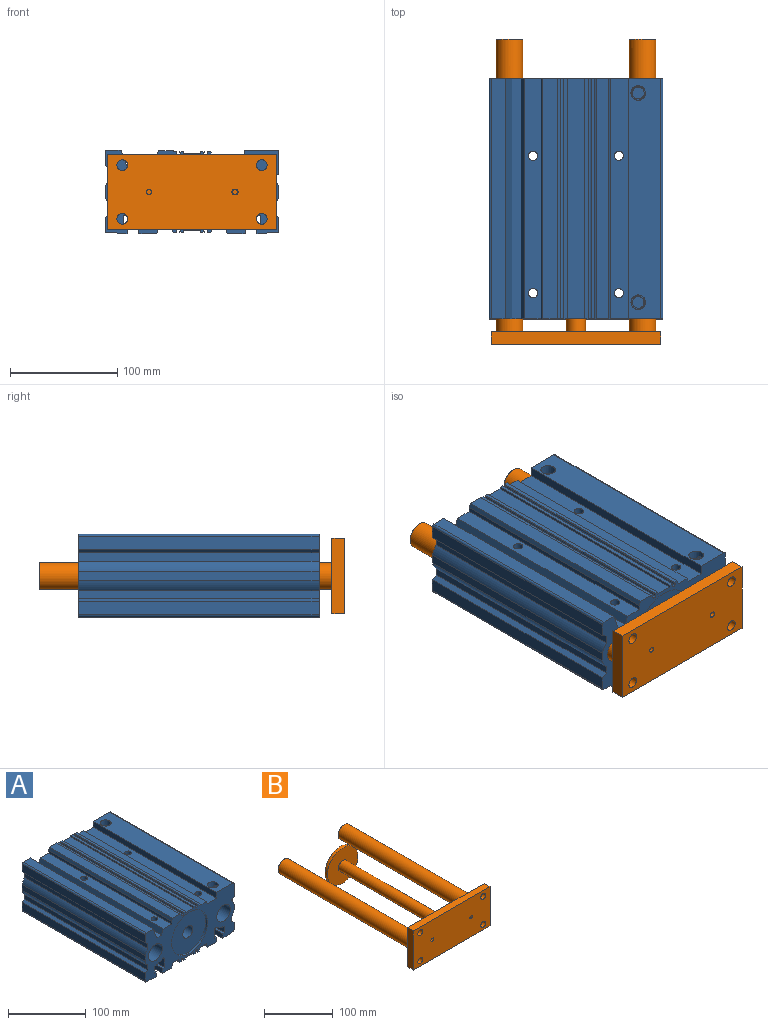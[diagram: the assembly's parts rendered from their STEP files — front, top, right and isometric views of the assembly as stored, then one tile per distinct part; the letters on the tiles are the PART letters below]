
ASSEMBLY  parts=2 mates=1
PART A: 165 faces, bbox 162.1x224.1x78.1 mm
  f0: cylinder r=4.3mm len=49mm, axis (0,0,1), area 1323.9mm2, adj f103,f137
  f1: cylinder r=4.3mm len=49mm, axis (0,0,1), area 1323.9mm2, adj f109,f135
  f2: cylinder r=4.3mm len=49mm, axis (0,0,1), area 1323.9mm2, adj f103,f133
  f3: cylinder r=4.3mm len=49mm, axis (0,0,1), area 1323.9mm2, adj f109,f131
  f4: plane 162x78mm, normal (0,-1,0), area 6470mm2, adj f6,f7,f8,f9,f10,f11,f12,f13
  f5: plane 162x78mm, normal (0,1,0), area 6312.6mm2, adj f6,f7,f8,f9,f10,f11,f12,f13
  f6: plane 224x12.5mm, normal (1,0,0), area 2800mm2, adj f4,f5,f69,f128
  f7: plane 224x9mm, normal (0,0,-1), area 2016mm2, adj f4,f5,f25,f125
  f8: plane 224x16.5mm, normal (0,0,-1), area 3519.3mm2, adj f4,f5,f34,f122,f134,f138,f139
  f9: plane 224x0.74mm, normal (-1,0,0), area 165.7mm2, adj f4,f5,f51,f119
  f10: plane 224x0.74mm, normal (1,0,0), area 165.7mm2, adj f4,f5,f51,f118
  f11: plane 224x2.2mm, normal (-1,0,0), area 492.8mm2, adj f4,f5,f59,f118
  f12: plane 224x8.78mm, normal (1,0,0), area 1965.6mm2, adj f4,f5,f67,f68
  f13: plane 224x8.78mm, normal (-1,0,0), area 1965.6mm2, adj f4,f5,f60,f63
  f14: plane 224x12.5mm, normal (-1,0,0), area 2800mm2, adj f4,f5,f65,f127
  f15: plane 224x16.5mm, normal (0,0,-1), area 3514.3mm2, adj f4,f5,f35,f114,f132,f136,f141,f142
  f16: plane 224x30mm, normal (0,0,1), area 6428.4mm2, adj f4,f5,f102,f129,f152,f156
  f17: plane 224x13mm, normal (0,0,1), area 2912mm2, adj f4,f5,f112,f130
  f18: plane 224x9mm, normal (0,0,-1), area 2016mm2, adj f4,f5,f44,f124
  f19: plane 224x20.5mm, normal (1,0,0), area 4296.5mm2, adj f4,f5,f66,f129,f160,f164
  f20: plane 224x12.5mm, normal (-1,0,0), area 2800mm2, adj f4,f5,f61,f130
  f21: cylinder r=12.53mm len=224mm, axis (0,-1,0), area 17628.1mm2, adj f4,f5
  f22: cylinder r=12.53mm len=224mm, axis (0,-1,0), area 17628.1mm2, adj f4,f5
  f23: cylinder r=2.5mm len=8mm, axis (0,1,0), area 125.7mm2, adj f5,f24
  f24: plane 5x5mm, normal (0,1,0), area 19.6mm2, adj f23
  f25: plane 224x7.5mm, normal (-1,0,0), area 1680mm2, adj f4,f5,f7,f26
  f26: plane 224x3.4mm, normal (0,0,1), area 761.6mm2, adj f4,f5,f25,f27
  f27: plane 224x10mm, normal (-1,0,0), area 2240mm2, adj f4,f5,f26,f28
  f28: plane 224x3.4mm, normal (0,0,-1), area 761.6mm2, adj f4,f5,f27,f29
  f29: plane 224x1.06mm, normal (-1,0,0), area 236.3mm2, adj f4,f5,f28,f30
  f30: cylinder r=20.5mm len=224mm, axis (0,1,0), area 2721.6mm2, adj f4,f5,f29,f31
  f31: cylinder r=2mm len=224mm, axis (0,1,0), area 1002mm2, adj f4,f5,f30,f32
  f32: plane 224x13.81mm, normal (1,0,0), area 3092.8mm2, adj f4,f5,f31,f33
  f33: plane 224x3.4mm, normal (0,0,1), area 761.6mm2, adj f4,f5,f32,f34
  f34: plane 224x7.5mm, normal (1,0,0), area 1680mm2, adj f4,f5,f8,f33
  f35: plane 224x7.5mm, normal (-1,0,0), area 1680mm2, adj f4,f5,f15,f36
  f36: plane 224x3.4mm, normal (0,0,1), area 761.6mm2, adj f4,f5,f35,f37
  f37: plane 224x13.81mm, normal (-1,0,0), area 3092.8mm2, adj f4,f5,f36,f38
  f38: cylinder r=2mm len=224mm, axis (0,1,0), area 1002mm2, adj f4,f5,f37,f39
  f39: cylinder r=20.5mm len=224mm, axis (0,1,0), area 2721.6mm2, adj f4,f5,f38,f40
  f40: plane 224x1.06mm, normal (1,0,0), area 236.3mm2, adj f4,f5,f39,f41
  f41: plane 224x3.4mm, normal (0,0,-1), area 761.6mm2, adj f4,f5,f40,f42
  f42: plane 224x10mm, normal (1,0,0), area 2240mm2, adj f4,f5,f41,f43
  f43: plane 224x3.4mm, normal (0,0,1), area 761.6mm2, adj f4,f5,f42,f44
  f44: plane 224x7.5mm, normal (1,0,0), area 1680mm2, adj f4,f5,f18,f43
  f45: cylinder r=2.02mm len=224mm, axis (0,-1,0), area 2093.3mm2, adj f4,f5,f46,f47
  f46: plane 224x0.74mm, normal (1,0,0), area 165.7mm2, adj f4,f5,f45,f104
  f47: plane 224x0.74mm, normal (-1,0,0), area 165.7mm2, adj f4,f5,f45,f97
  f48: cylinder r=2.02mm len=224mm, axis (0,-1,0), area 2093.3mm2, adj f4,f5,f49,f50
  f49: plane 224x0.74mm, normal (1,0,0), area 165.7mm2, adj f4,f5,f48,f96
  f50: plane 224x0.74mm, normal (-1,0,0), area 165.7mm2, adj f4,f5,f48,f98
  f51: cylinder r=2.02mm len=224mm, axis (0,-1,0), area 2093.3mm2, adj f4,f5,f9,f10
  f52: cylinder r=2.02mm len=224mm, axis (0,-1,0), area 2093.3mm2, adj f4,f5,f53,f54
  f53: plane 224x0.74mm, normal (-1,0,0), area 165.7mm2, adj f4,f5,f52,f113
  f54: plane 224x0.74mm, normal (1,0,0), area 165.7mm2, adj f4,f5,f52,f117
  f55: plane 224x2.2mm, normal (1,0,0), area 492.8mm2, adj f4,f5,f57,f97
  f56: plane 224x2.2mm, normal (-1,0,0), area 492.8mm2, adj f4,f5,f57,f96
  f57: plane 224x16mm, normal (0,0,1), area 3584mm2, adj f4,f5,f55,f56
  f58: plane 224x2.2mm, normal (1,0,0), area 492.8mm2, adj f4,f5,f59,f113
  f59: plane 224x16mm, normal (0,0,-1), area 3584mm2, adj f4,f5,f11,f58
  f60: cylinder r=19.5mm len=224mm, axis (0,-1,0), area 2371.8mm2, adj f4,f5,f13,f62
  f61: plane 224x5mm, normal (-0.5,0,-0.87), area 1293.3mm2, adj f4,f5,f20,f62
  f62: plane 224x8.04mm, normal (-1,0,0), area 1800.8mm2, adj f4,f5,f60,f61
  f63: cylinder r=19.5mm len=224mm, axis (0,-1,0), area 2371.8mm2, adj f4,f5,f13,f64
  f64: plane 224x7.04mm, normal (-1,0,0), area 1576.8mm2, adj f4,f5,f63,f65
  f65: plane 224x5mm, normal (-0.5,0,0.87), area 1293.3mm2, adj f4,f5,f14,f64
  f66: plane 224x2.93mm, normal (0.5,0,-0.87), area 758.5mm2, adj f4,f5,f19,f71
  f67: cylinder r=19.5mm len=224mm, axis (0,-1,0), area 1864.1mm2, adj f4,f5,f12,f71
  f68: cylinder r=19.5mm len=224mm, axis (0,-1,0), area 2371.8mm2, adj f4,f5,f12,f70
  f69: plane 224x5mm, normal (0.5,0,0.87), area 1293.3mm2, adj f4,f5,f6,f70
  f70: plane 224x7.04mm, normal (1,0,0), area 1576.8mm2, adj f4,f5,f68,f69
  f71: cylinder r=2mm len=224mm, axis (0,-1,0), area 762mm2, adj f4,f5,f66,f67
  f72: cylinder r=31.5mm len=63mm, axis (0,1,0), area 613.6mm2, adj f5,f73
  f73: plane 63x63mm, normal (0,1,0), area 3117.2mm2, adj f72
  f74: cylinder r=32.5mm len=65mm, axis (0,-1,0), area 633mm2, adj f4,f75
  f75: plane 65x65mm, normal (0,-1,0), area 3062.4mm2, adj f74,f79
  f76: plane 63x63mm, normal (0,-1,0), area 3117.2mm2, adj f77
  f77: cylinder r=31.5mm len=180mm, axis (0,-1,0), area 35625.7mm2, adj f76,f78
  f78: plane 63x63mm, normal (0,1,0), area 2861.4mm2, adj f77,f79
  f79: cylinder r=9.03mm len=18.9mm, axis (0,1,0), area 1071.7mm2, adj f75,f78
  f80: cylinder r=5mm len=22mm, axis (0,1,0), area 691.2mm2, adj f5,f81
  f81: plane 10x10mm, normal (0,1,0), area 78.5mm2, adj f80
  f82: cylinder r=5mm len=22mm, axis (0,1,0), area 691.2mm2, adj f5,f83
  f83: plane 10x10mm, normal (0,1,0), area 78.5mm2, adj f82
  f84: cylinder r=5mm len=22mm, axis (0,1,0), area 691.2mm2, adj f5,f85
  f85: plane 10x10mm, normal (0,1,0), area 78.5mm2, adj f84
  f86: cylinder r=5mm len=22mm, axis (0,1,0), area 691.2mm2, adj f5,f87
  f87: plane 10x10mm, normal (0,1,0), area 78.5mm2, adj f86
  f88: plane 4x1mm, normal (0,0,-1), area 4mm2, adj f5,f90,f91,f92,f93
  f89: plane 4x1mm, normal (0,0,1), area 4mm2, adj f5,f90,f91,f92,f93
  f90: plane 5x3mm, normal (0,1,0), area 2.5mm2, adj f88,f89,f92,f95
  f91: plane 5x3mm, normal (0,1,0), area 2.5mm2, adj f88,f89,f93,f95
  f92: cylinder r=2.5mm len=5mm, axis (0,1,0), area 31.4mm2, adj f5,f88,f89,f90
  f93: cylinder r=2.5mm len=5mm, axis (0,1,0), area 31.4mm2, adj f5,f88,f89,f91
  f94: plane 5x5mm, normal (0,1,0), area 19.6mm2, adj f95
  f95: cylinder r=2.5mm len=5mm, axis (0,1,0), area 62.8mm2, adj f90,f91,f94
  f96: plane 224x3.2mm, normal (0,0,1), area 716.8mm2, adj f4,f5,f49,f56
  f97: plane 224x3.2mm, normal (0,0,1), area 716.8mm2, adj f4,f5,f47,f55
  f98: plane 224x3.2mm, normal (0,0,1), area 716.8mm2, adj f4,f5,f50,f99
  f99: plane 224x3.7mm, normal (0.94,0,0.34), area 882mm2, adj f4,f5,f98,f100
  f100: plane 224x11.75mm, normal (0,0,1), area 2632.7mm2, adj f4,f5,f99,f101
  f101: plane 224x4mm, normal (0.94,0,0.34), area 953.5mm2, adj f4,f5,f100,f103
  f102: plane 224x9mm, normal (-1,0,0), area 2016mm2, adj f4,f5,f16,f103
  f103: plane 224x17.04mm, normal (0,0,1), area 3701.7mm2, adj f0,f2,f4,f5,f101,f102
  f104: plane 224x3.2mm, normal (0,0,1), area 716.8mm2, adj f4,f5,f46,f105
  f105: plane 224x0.8mm, normal (1,0,0), area 179.2mm2, adj f4,f5,f104,f106
  f106: plane 224x13.6mm, normal (0,0,1), area 3046.4mm2, adj f4,f5,f105,f107
  f107: plane 224x4.12mm, normal (-0.94,0,0.34), area 982.4mm2, adj f4,f5,f106,f108
  f108: plane 224x4.38mm, normal (-1,0,0), area 980.8mm2, adj f4,f5,f107,f109
  f109: plane 224x15.5mm, normal (0,0,1), area 3355.8mm2, adj f1,f3,f4,f5,f108,f110
  f110: plane 224x8mm, normal (-0.94,0,0.34), area 1907mm2, adj f4,f5,f109,f111
  f111: plane 224x8.9mm, normal (0,0,1), area 1993.8mm2, adj f4,f5,f110,f112
  f112: plane 224x17mm, normal (0.94,0,0.34), area 4052.4mm2, adj f4,f5,f17,f111
  f113: plane 224x3.2mm, normal (0,0,-1), area 716.8mm2, adj f4,f5,f53,f58
  f114: plane 224x6.5mm, normal (0.94,0,-0.34), area 1549.4mm2, adj f4,f5,f15,f115
  f115: plane 224x11.34mm, normal (0,0,-1), area 2540.5mm2, adj f4,f5,f114,f116
  f116: plane 224x5.2mm, normal (-0.94,0,-0.34), area 1239.6mm2, adj f4,f5,f115,f117
  f117: plane 224x3.2mm, normal (0,0,-1), area 716.8mm2, adj f4,f5,f54,f116
  f118: plane 224x3.2mm, normal (0,0,-1), area 716.8mm2, adj f4,f5,f10,f11
  f119: plane 224x3.2mm, normal (0,0,-1), area 716.8mm2, adj f4,f5,f9,f120
  f120: plane 224x5.2mm, normal (0.94,0,-0.34), area 1239.6mm2, adj f4,f5,f119,f121
  f121: plane 224x11.34mm, normal (0,0,-1), area 2540.5mm2, adj f4,f5,f120,f122
  f122: plane 224x6.5mm, normal (-0.94,0,-0.34), area 1549.4mm2, adj f4,f5,f8,f121
  f123: plane 224x8.92mm, normal (0,0,-1), area 1998.7mm2, adj f4,f5,f124,f127
  f124: plane 224x1mm, normal (-0.87,0,-0.5), area 258.7mm2, adj f4,f5,f18,f123
  f125: plane 224x1mm, normal (0.87,0,-0.5), area 258.7mm2, adj f4,f5,f7,f126
  f126: plane 224x8.92mm, normal (0,0,-1), area 1998.7mm2, adj f4,f5,f125,f128
  f127: cylinder r=2mm len=224mm, axis (0,-1,0), area 703.7mm2, adj f4,f5,f14,f123
  f128: cylinder r=2mm len=224mm, axis (0,1,0), area 703.7mm2, adj f4,f5,f6,f126
  f129: cylinder r=2mm len=224mm, axis (0,1,0), area 703.7mm2, adj f4,f5,f16,f19
  f130: cylinder r=2mm len=224mm, axis (0,1,0), area 703.7mm2, adj f4,f5,f17,f20
  f131: plane 10x10mm, normal (0,0,-1), area 20.5mm2, adj f3,f132
  f132: cylinder r=5mm len=20mm, axis (0,0,-1), area 628.3mm2, adj f15,f131
  f133: plane 10x10mm, normal (0,0,-1), area 20.5mm2, adj f2,f134
  f134: cylinder r=5mm len=20mm, axis (0,0,-1), area 628.3mm2, adj f8,f133
  f135: plane 10x10mm, normal (0,0,-1), area 20.5mm2, adj f1,f136
  f136: cylinder r=5mm len=20mm, axis (0,0,-1), area 628.3mm2, adj f15,f135
  f137: plane 10x10mm, normal (0,0,-1), area 20.5mm2, adj f0,f138
  f138: cylinder r=5mm len=20mm, axis (0,0,-1), area 628.3mm2, adj f8,f137
  f139: cylinder r=2.5mm len=8mm, axis (0,0,-1), area 125.7mm2, adj f8,f140
  f140: plane 5x5mm, normal (0,0,-1), area 19.6mm2, adj f139
  f141: plane 4x1mm, normal (0,1,0), area 4mm2, adj f15,f143,f144,f145,f146
  f142: plane 4x1mm, normal (0,-1,0), area 4mm2, adj f15,f143,f144,f145,f146
  f143: plane 5x3mm, normal (0,0,-1), area 2.5mm2, adj f141,f142,f145,f148
  f144: plane 5x3mm, normal (0,0,-1), area 2.5mm2, adj f141,f142,f146,f148
  f145: cylinder r=2.5mm len=5mm, axis (0,0,-1), area 31.4mm2, adj f15,f141,f142,f143
  f146: cylinder r=2.5mm len=5mm, axis (0,0,-1), area 31.4mm2, adj f15,f141,f142,f144
  f147: plane 5x5mm, normal (0,0,-1), area 19.6mm2, adj f148
  f148: cylinder r=2.5mm len=5mm, axis (0,0,-1), area 62.8mm2, adj f143,f144,f147
  f149: plane 11.13x11.13mm, normal (0,0,1), area 97.2mm2, adj f150
  f150: cylinder r=5.56mm len=11.13mm, axis (0,0,1), area 246.4mm2, adj f149,f151
  f151: plane 13.12x13.12mm, normal (0,0,1), area 37.9mm2, adj f150,f152
  f152: cone r=6.81mm half-angle=1.7deg, axis (0,0,1), area 357.2mm2, adj f16,f151
  f153: plane 11.13x10.99mm, normal (0,0,1), area 96.8mm2, adj f154,f162
  f154: cylinder r=5.56mm len=11.13mm, axis (0,0,1), area 204.6mm2, adj f153,f155,f162
  f155: plane 13.19x11.96mm, normal (0,0,1), area 30.9mm2, adj f154,f156,f162
  f156: cone r=6.81mm half-angle=1.7deg, axis (0,0,1), area 337.9mm2, adj f16,f155,f161,f162
  f157: cone r=5.56mm half-angle=59deg, axis (1,0,0), area 113.4mm2, adj f158
  f158: cylinder r=5.56mm len=11.13mm, axis (1,0,0), area 246.4mm2, adj f157,f159
  f159: plane 13.12x13.12mm, normal (1,0,0), area 37.9mm2, adj f158,f160
  f160: cone r=6.86mm half-angle=1.7deg, axis (1,0,0), area 422.5mm2, adj f19,f159
  f161: cylinder r=5.56mm len=11.13mm, axis (1,0,0), area 243.4mm2, adj f156,f162,f163
  f162: cone r=5.56mm half-angle=59deg, axis (1,0,0), area 45.2mm2, adj f153,f154,f155,f156,f161
  f163: plane 13.12x13.12mm, normal (1,0,0), area 37.9mm2, adj f161,f164
  f164: cone r=6.86mm half-angle=1.7deg, axis (1,0,0), area 422.5mm2, adj f19,f163
PART B: 30 faces, bbox 158x284.5x70 mm
  f0: cylinder r=31.45mm len=62.9mm, axis (0,1,0), area 988mm2, adj f1,f2
  f1: plane 62.9x62.9mm, normal (0,-1,0), area 2852.9mm2, adj f0,f3
  f2: plane 62.9x62.9mm, normal (0,1,0), area 3107.4mm2, adj f0
  f3: cylinder r=9mm len=213mm, axis (0,1,0), area 12044.9mm2, adj f1,f9
  f4: plane 70x12mm, normal (-1,0,0), area 840mm2, adj f5,f7,f8,f9
  f5: plane 158x12mm, normal (0,0,-1), area 1896mm2, adj f4,f6,f8,f9
  f6: plane 70x12mm, normal (1,0,0), area 840mm2, adj f5,f7,f8,f9
  f7: plane 158x12mm, normal (0,0,1), area 1896mm2, adj f4,f6,f8,f9
  f8: plane 158x70mm, normal (0,-1,0), area 10701.6mm2, adj f4,f5,f6,f7,f14,f18,f19,f20
  f9: plane 158x70mm, normal (0,1,0), area 9509.6mm2, adj f3,f4,f5,f6,f7,f10,f12,f18
  f10: cylinder r=12.5mm len=272mm, axis (0,-1,0), area 21362.8mm2, adj f9,f16
  f11: plane 24x24mm, normal (0,1,0), area 452.4mm2, adj f16
  f12: cylinder r=12.5mm len=272mm, axis (0,-1,0), area 21362.8mm2, adj f9,f17
  f13: plane 24x24mm, normal (0,1,0), area 452.4mm2, adj f17
  f14: cylinder r=2.5mm len=8mm, axis (0,-1,0), area 125.7mm2, adj f8,f15
  f15: plane 5x5mm, normal (0,-1,0), area 19.6mm2, adj f14
  f16: cone r=12mm half-angle=45deg, axis (0,-1,0), area 54.4mm2, adj f10,f11
  f17: cone r=12mm half-angle=45deg, axis (0,-1,0), area 54.4mm2, adj f12,f13
  f18: cylinder r=5mm len=12mm, axis (0,-1,0), area 377mm2, adj f8,f9
  f19: cylinder r=5mm len=12mm, axis (0,-1,0), area 377mm2, adj f8,f9
  f20: cylinder r=5mm len=12mm, axis (0,-1,0), area 377mm2, adj f8,f9
  f21: cylinder r=5mm len=12mm, axis (0,-1,0), area 377mm2, adj f8,f9
  f22: plane 4x1mm, normal (0,0,1), area 4mm2, adj f8,f24,f25,f26,f27
  f23: plane 4x1mm, normal (0,0,-1), area 4mm2, adj f8,f24,f25,f26,f27
  f24: plane 5x3mm, normal (0,-1,0), area 2.5mm2, adj f22,f23,f27,f29
  f25: plane 5x3mm, normal (0,-1,0), area 2.5mm2, adj f22,f23,f26,f29
  f26: cylinder r=2.5mm len=5mm, axis (0,-1,0), area 31.4mm2, adj f8,f22,f23,f25
  f27: cylinder r=2.5mm len=5mm, axis (0,-1,0), area 31.4mm2, adj f8,f22,f23,f24
  f28: plane 5x5mm, normal (0,-1,0), area 19.6mm2, adj f29
  f29: cylinder r=2.5mm len=5mm, axis (0,-1,0), area 62.8mm2, adj f24,f25,f28
PLACE A t=(0,112,0)mm
PLACE B rot(axis=(0,1,0),180deg) t=(0,116.1,0)mm
MATE slider B.f0 <-> A.f72  axis (0,1,0) through (0,-11.9,0)mm
